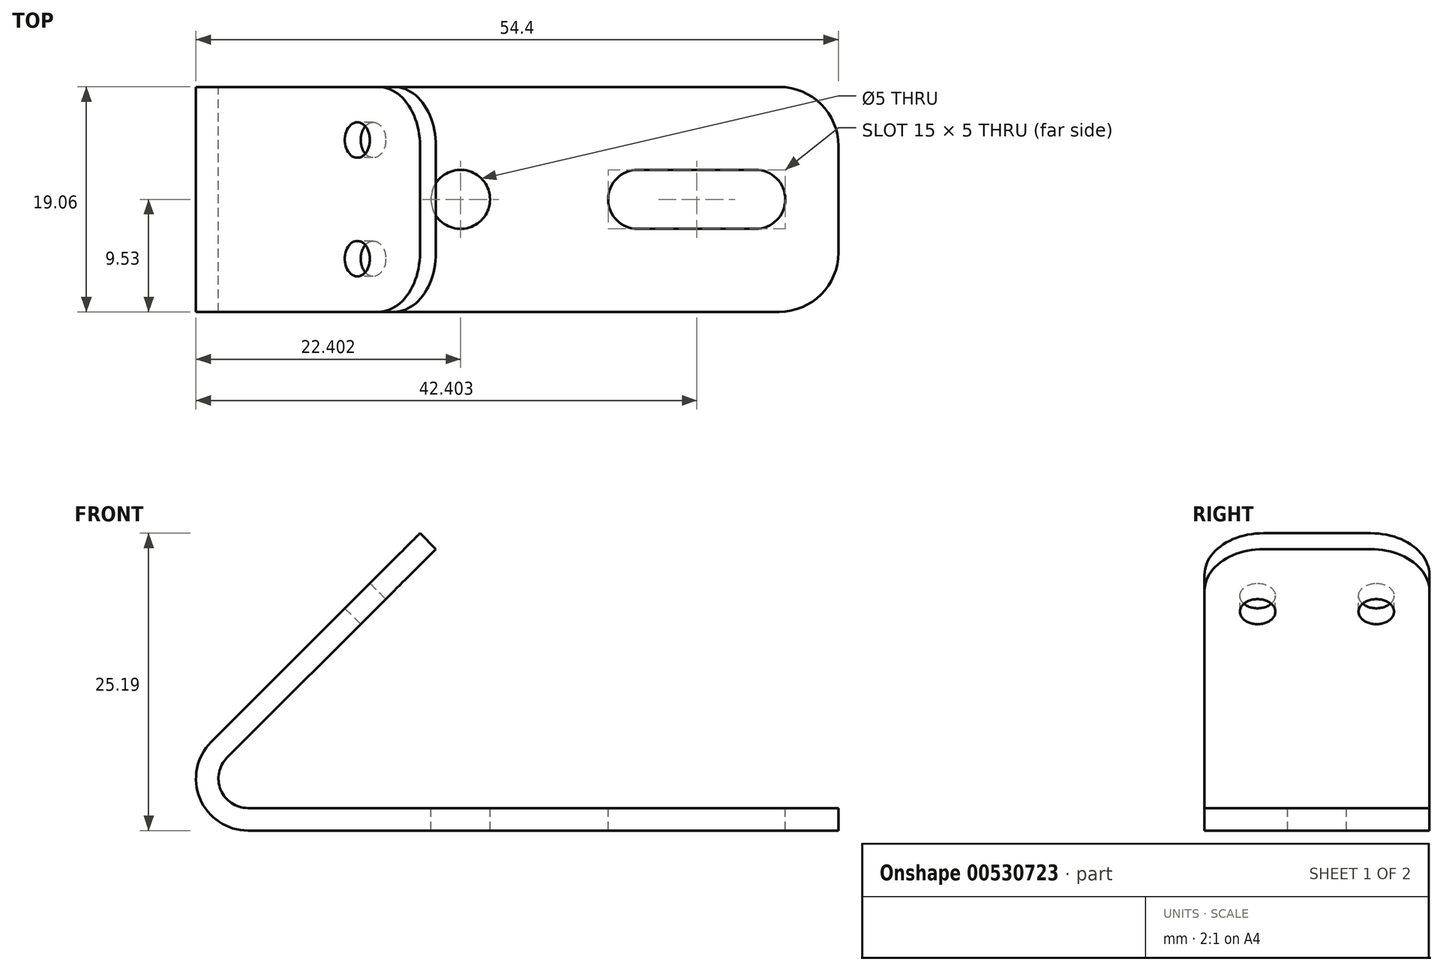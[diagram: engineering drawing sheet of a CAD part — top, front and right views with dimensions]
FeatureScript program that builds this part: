
annotation { "Feature Type Name" : "Feature", "Feature Type Description" : "" }
export const myFeature = defineFeature(function(context is Context, id is Id, definition is map)
    precondition{}
    {
        {
            var Q0;
            Q0=qCreatedBy(makeId("Front.planeOp"),FACE);
            var sketch = newSketch(context, id + "F0", { "sketchPlane" : qUnion([Q0])});
            skLineSegment(sketch, "E0", {"start": v(10.62, 0) * mm, "end": v(60.62, 0) * mm});
            skLineSegment(sketch, "E1", {"start": v(60.62, 0) * mm, "end": v(60.62, 1.9) * mm});
            skLineSegment(sketch, "E2", {"start": v(60.62, 1.9) * mm, "end": v(0, 1.9) * mm});
            skLineSegment(sketch, "E3", {"start": v(7.51, 7.51) * mm, "end": v(25.19, 25.19) * mm});
            skPoint(sketch, "E4.visualSharp", {"position": v(0, 0) * mm});
            skArc(sketch, "E4.filletArc", {"start": v(7.51, 7.51) * mm, "mid": v(6.56, 2.72) * mm, "end": v(10.62, 0) * mm});
            skLineSegment(sketch, "E5", {"start": v(25.19, 25.19) * mm, "end": v(26.53, 23.85) * mm});
            skLineSegment(sketch, "E6", {"start": v(26.53, 23.85) * mm, "end": v(8.85, 6.17) * mm});
            skArc(sketch, "E7", {"start": v(8.85, 6.17) * mm, "mid": v(8.31, 3.44) * mm, "end": v(10.62, 1.9) * mm});
            skSolve(sketch);
        }
        {
            var Q0;
            Q0=qSketchRegion(id+"F0",true);
            extrude(context, id + "F1", {"entities" : qUnion([Q0]), "endBound" : BoundingType.SYMMETRIC, "depth" : 19.05 * mm});
        }
        {
            var Q0;
            Q0=makeQuery(id+"F1.opExtrude","SWEPT_FACE",FACE,{"disambiguationData":[OSD([sQuery(id+"F0.wireOp",EDGE,"E2")])]});
            var sketch = newSketch(context, id + "F2", { "sketchPlane" : qUnion([Q0])});
            skLineSegment(sketch, "E8.0", {"start": v(60.62, -9.53) * mm, "end": v(60.62, 9.52) * mm});
            skLineSegment(sketch, "E9.0", {"start": v(60.62, 9.53) * mm, "end": v(10.62, 9.53) * mm});
            skLineSegment(sketch, "E10.0", {"start": v(60.62, -9.53) * mm, "end": v(10.62, -9.53) * mm});
            skLineSegment(sketch, "E11", {"start": v(60.62, 0) * mm, "end": v(56.12, 0) * mm});
            skLineSegment(sketch, "E12", {"start": v(56.12, 0) * mm, "end": v(41.12, 0) * mm});
            skLineSegment(sketch, "E13", {"start": v(56.12, 0) * mm, "end": v(56.12, 2.5) * mm});
            skCircle(sketch, "E14", {"center": v(53.62, 0) * mm, "radius": 2.5 * mm});
            skCircle(sketch, "E15", {"center": v(43.62, 0) * mm, "radius": 2.5 * mm});
            skLineSegment(sketch, "E16", {"start": v(43.62, 2.5) * mm, "end": v(53.62, 2.5) * mm});
            skLineSegment(sketch, "E17", {"start": v(43.62, -2.5) * mm, "end": v(53.62, -2.5) * mm});
            skCircle(sketch, "E18", {"center": v(28.62, 0) * mm, "radius": 2.5 * mm});
            skSolve(sketch);
        }
        {
            var Q0;
            Q0=qSketchRegion(id+"F2",true);
            extrude(context, id + "F3", {"entities" : qUnion([Q0]), "operationType" : NewBodyOperationType.REMOVE, "endBound" : BoundingType.THROUGH_ALL, "oppositeDirection" : true, "depth" : 25 * mm});
        }
        {
            var Q0;
            Q0=makeQuery(id+"F1.opExtrude","SWEPT_FACE",FACE,{"disambiguationData":[OSD([sQuery(id+"F0.wireOp",EDGE,"E3")])]});
            var sketch = newSketch(context, id + "F4", { "sketchPlane" : qUnion([Q0])});
            skLineSegment(sketch, "E19.0", {"start": v(9.53, 35.62) * mm, "end": v(-9.52, 35.62) * mm});
            skLineSegment(sketch, "E19.1", {"start": v(9.53, 10.62) * mm, "end": v(-9.52, 10.62) * mm});
            skLineSegment(sketch, "E19.2", {"start": v(-9.53, 10.62) * mm, "end": v(-9.53, 35.62) * mm});
            skLineSegment(sketch, "E19.3", {"start": v(9.53, 10.62) * mm, "end": v(9.53, 35.62) * mm});
            skLineSegment(sketch, "E20", {"start": v(-9.53, 35.62) * mm, "end": v(-9.53, 28.12) * mm});
            skCircle(sketch, "E21", {"center": v(-5.03, 28.12) * mm, "radius": 1.5 * mm});
            skLineSegment(sketch, "E22", {"start": v(9.53, 6.22) * mm, "end": v(-9.52, 6.22) * mm});
            skCircle(sketch, "E23", {"center": v(5.03, 28.12) * mm, "radius": 1.5 * mm});
            skSolve(sketch);
        }
        {
            var Q0;
            Q0=makeQuery(id+"F4.imprint","IMPRINT",FACE,{"disambiguationData":[TD([[makeQuery(id+"F4.imprint","IMPRINT",EDGE,{"derivedFrom":sQuery(id+"F4.wireOp",EDGE,"E21")}),1.0]])]});
            var Q1;
            Q1=makeQuery(id+"F4.imprint","IMPRINT",FACE,{"disambiguationData":[TD([[makeQuery(id+"F4.imprint","IMPRINT",EDGE,{"derivedFrom":sQuery(id+"F4.wireOp",EDGE,"E23")}),1.0]])]});
            extrude(context, id + "F5", {"entities" : qUnion([Q0, Q1]), "operationType" : NewBodyOperationType.REMOVE, "endBound" : BoundingType.UP_TO_NEXT, "oppositeDirection" : true, "depth" : 25 * mm});
        }
        {
            var Q0;
            Q0=makeQuery(id+"F1.opExtrude","CAP_EDGE",EDGE,{"disambiguationData":[OSD([sQuery(id+"F0.wireOp",EDGE,"E5")])],"isStart":true});
            var Q1;
            Q1=makeQuery(id+"F1.opExtrude","CAP_EDGE",EDGE,{"disambiguationData":[OSD([sQuery(id+"F0.wireOp",EDGE,"E5")])],"isStart":false});
            var Q2;
            Q2=makeQuery(id+"F1.opExtrude","CAP_EDGE",EDGE,{"disambiguationData":[OSD([sQuery(id+"F0.wireOp",EDGE,"E1")])],"isStart":false});
            var Q3;
            Q3=makeQuery(id+"F1.opExtrude","CAP_EDGE",EDGE,{"disambiguationData":[OSD([sQuery(id+"F0.wireOp",EDGE,"E1")])],"isStart":true});
            fillet(context, id + "F6", {"entities" : qUnion([Q0, Q1, Q2, Q3]), "radius" : 5 * mm, "tangentPropagation" : true, "allowEdgeOverflow" : false});
        }
    });
